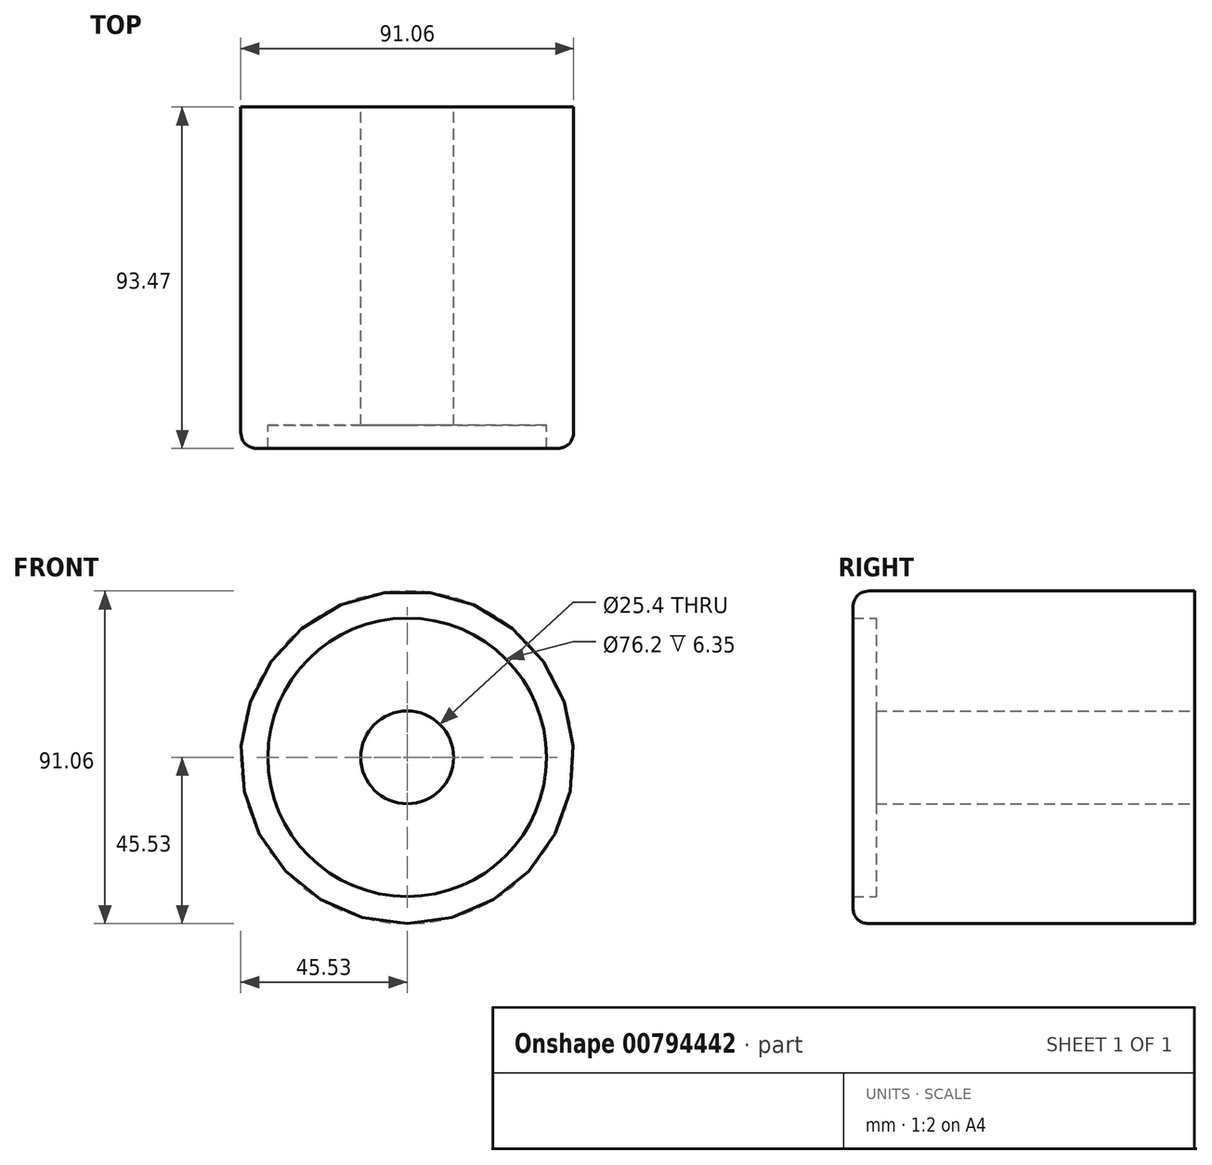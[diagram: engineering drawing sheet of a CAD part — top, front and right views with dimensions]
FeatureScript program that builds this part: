
annotation { "Feature Type Name" : "Feature", "Feature Type Description" : "" }
export const myFeature = defineFeature(function(context is Context, id is Id, definition is map)
    precondition{}
    {
        {
            var Q0;
            Q0=qCreatedBy(makeId("Front.planeOp"),FACE);
            var sketch = newSketch(context, id + "F0", { "sketchPlane" : qUnion([Q0])});
            skCircle(sketch, "E0", {"center": v(0, 0) * mm, "radius": 45.53 * mm});
            skSolve(sketch);
        }
        {
            var Q0;
            Q0=makeQuery(id+"F0.imprint","IMPRINT",FACE,{"disambiguationData":[TD([[makeQuery(id+"F0.imprint","IMPRINT",EDGE,{"derivedFrom":sQuery(id+"F0.wireOp",EDGE,"E0")}),1.0]])]});
            extrude(context, id + "F1", {"entities" : qUnion([Q0]), "depth" : 93.47 * mm, "offsetDistance" : 25.4 * mm});
        }
        {
            var Q0;
            Q0=makeQuery(id+"F1.opExtrude","CAP_FACE",FACE,{"disambiguationData":[OSD([sQuery(id+"F0.wireOp",EDGE,"E0")])],"isStart":false});
            var sketch = newSketch(context, id + "F2", { "sketchPlane" : qUnion([Q0])});
            skCircle(sketch, "E1", {"center": v(0, 0) * mm, "radius": 25.86 * mm});
            skSolve(sketch);
        }
        {
            var Q0;
            Q0=sQuery(id+"F2.wireOp",VERTEX,"E1.center");
            var Q1;
            Q1=makeQuery(id+"F1.opExtrude","SWEPT_BODY",BODY,{"disambiguationData":[OSD([sQuery(id+"F0.wireOp",EDGE,"E0")])]});
            hole(context, id + "F3", {"style" : HoleStyle.C_BORE, "endStyle" : HoleEndStyle.THROUGH, "holeDiameter" : 25.4 * mm, "cBoreDiameter" : 76.2 * mm, "cBoreDepth" : 6.35 * mm, "majorDiameter" : 6.35 * mm, "isTappedThrough" : true, "tappedDepth" : 12.7 * mm, "tapClearance" : 3, "locations" : qUnion([Q0]), "scope" : qUnion([Q1])});
        }
        {
            var Q0;
            Q0=makeQuery(id+"F1.opExtrude","CAP_EDGE",EDGE,{"disambiguationData":[OSD([sQuery(id+"F0.wireOp",EDGE,"E0")])],"isStart":false});
            fillet(context, id + "F4", {"entities" : qUnion([Q0]), "radius" : 5.08 * mm, "tangentPropagation" : true, "rho" : 0.5, "crossSection" : FilletCrossSection.CONIC, "allowEdgeOverflow" : false});
        }
    });
